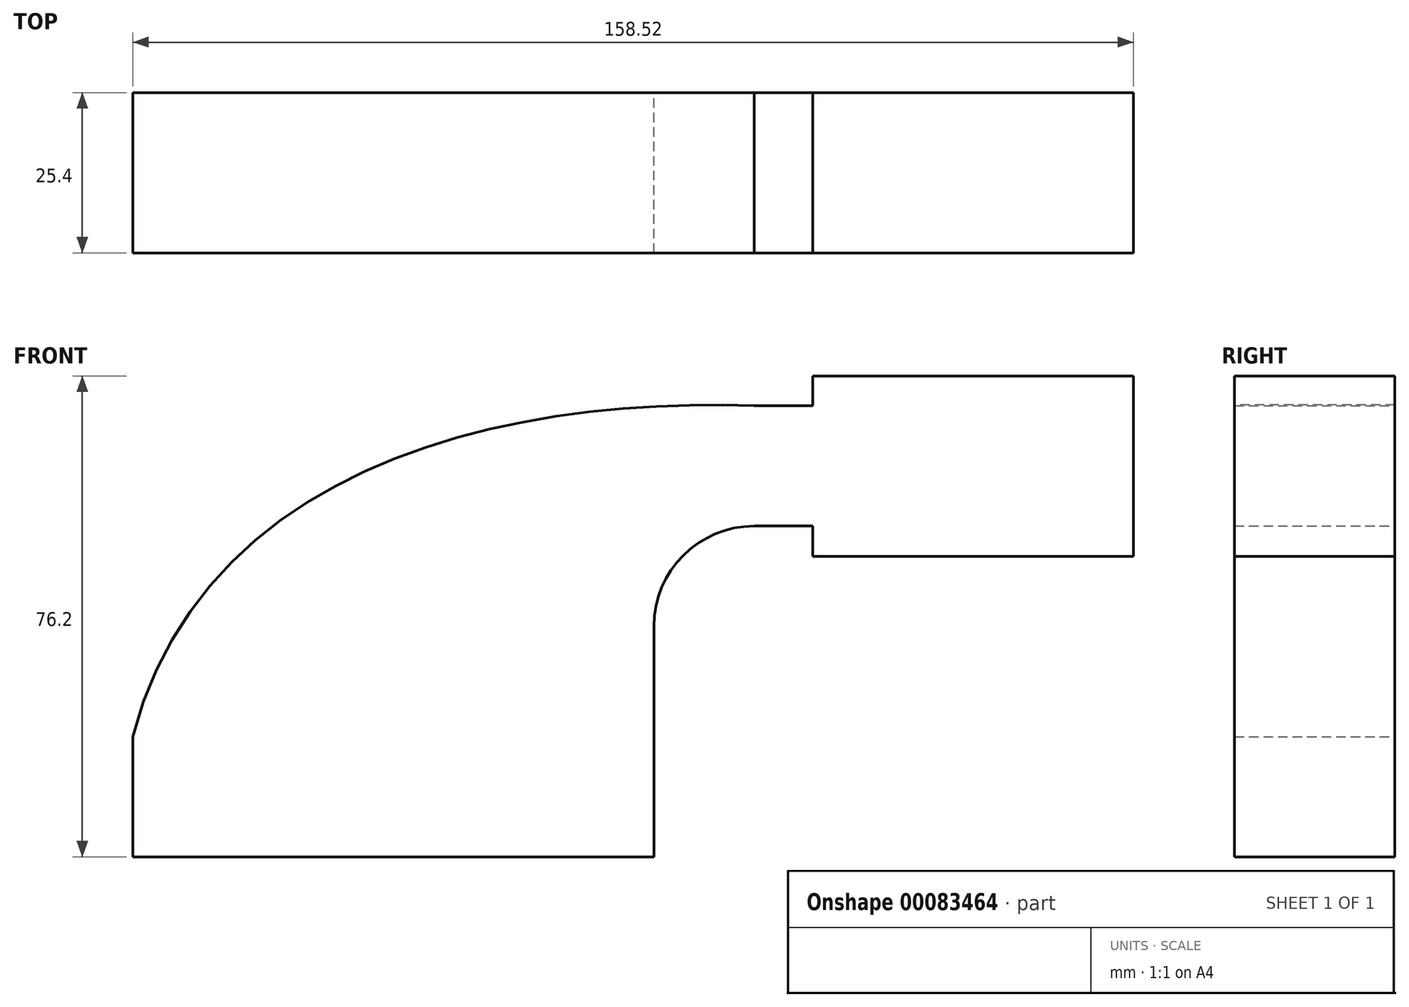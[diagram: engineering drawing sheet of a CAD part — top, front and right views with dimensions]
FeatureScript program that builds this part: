
annotation { "Feature Type Name" : "Feature", "Feature Type Description" : "" }
export const myFeature = defineFeature(function(context is Context, id is Id, definition is map)
    precondition{}
    {
        {
            var Q0;
            Q0=qCreatedBy(makeId("Front.planeOp"),FACE);
            var sketch = newSketch(context, id + "F0", { "sketchPlane" : qUnion([Q0])});
            skLineSegment(sketch, "E0.bottom", {"start": v(-75.84, 0) * mm, "end": v(6.7, 0) * mm});
            skLineSegment(sketch, "E0.top", {"start": v(-75.84, -19.05) * mm, "end": v(6.7, -19.05) * mm});
            skLineSegment(sketch, "E0.left", {"start": v(-75.84, 0) * mm, "end": v(-75.84, -19.05) * mm});
            skLineSegment(sketch, "E0.right", {"start": v(6.7, 0) * mm, "end": v(6.7, -19.05) * mm});
            skPoint(sketch, "E0.middle", {"position": v(-34.57, -9.53) * mm});
            skLineSegment(sketch, "E1.bottom", {"start": v(82.68, 28.58) * mm, "end": v(31.88, 28.57) * mm});
            skLineSegment(sketch, "E1.top", {"start": v(82.68, 57.15) * mm, "end": v(31.88, 57.15) * mm});
            skLineSegment(sketch, "E1.left", {"start": v(82.68, 28.58) * mm, "end": v(82.68, 57.15) * mm});
            skLineSegment(sketch, "E1.right", {"start": v(31.88, 28.57) * mm, "end": v(31.88, 57.15) * mm});
            skPoint(sketch, "E1.middle", {"position": v(57.28, 42.86) * mm});
            skLineSegment(sketch, "E2", {"start": v(6.7, 0) * mm, "end": v(6.7, 17.48) * mm});
            skArc(sketch, "E3", {"start": v(6.7, 17.48) * mm, "mid": v(11.36, 28.7) * mm, "end": v(22.58, 33.35) * mm});
            skLineSegment(sketch, "E4", {"start": v(22.58, 33.35) * mm, "end": v(50, 33.35) * mm});
            skLineSegment(sketch, "E5.0", {"start": v(22.58, 52.4) * mm, "end": v(50, 52.4) * mm});
            skArc(sketch, "E5.1", {"start": v(-12.34, 17.48) * mm, "mid": v(-2.11, 42.17) * mm, "end": v(22.58, 52.4) * mm});
            skLineSegment(sketch, "E5.2", {"start": v(-12.34, 0) * mm, "end": v(-12.34, 17.48) * mm});
            skLineSegment(sketch, "E6", {"start": v(57.28, 28.57) * mm, "end": v(57.28, 57.15) * mm});
            skFitSpline(sketch, "E7", {"points": [v(-75.84, 0) * mm, v(22.58, 52.4) * mm], "startDerivative": vector(34.2, 130.32) * mm, "endDerivative": vector(115.33, -4.4) * mm});
            skSolve(sketch);
        }
        {
            var Q0;
            Q0 = qSketchRegion(id + "F0", true);
            extrude(context, id + "F1", {"entities" : qUnion([Q0]), "depth" : 25.4 * mm});
        }
    });
